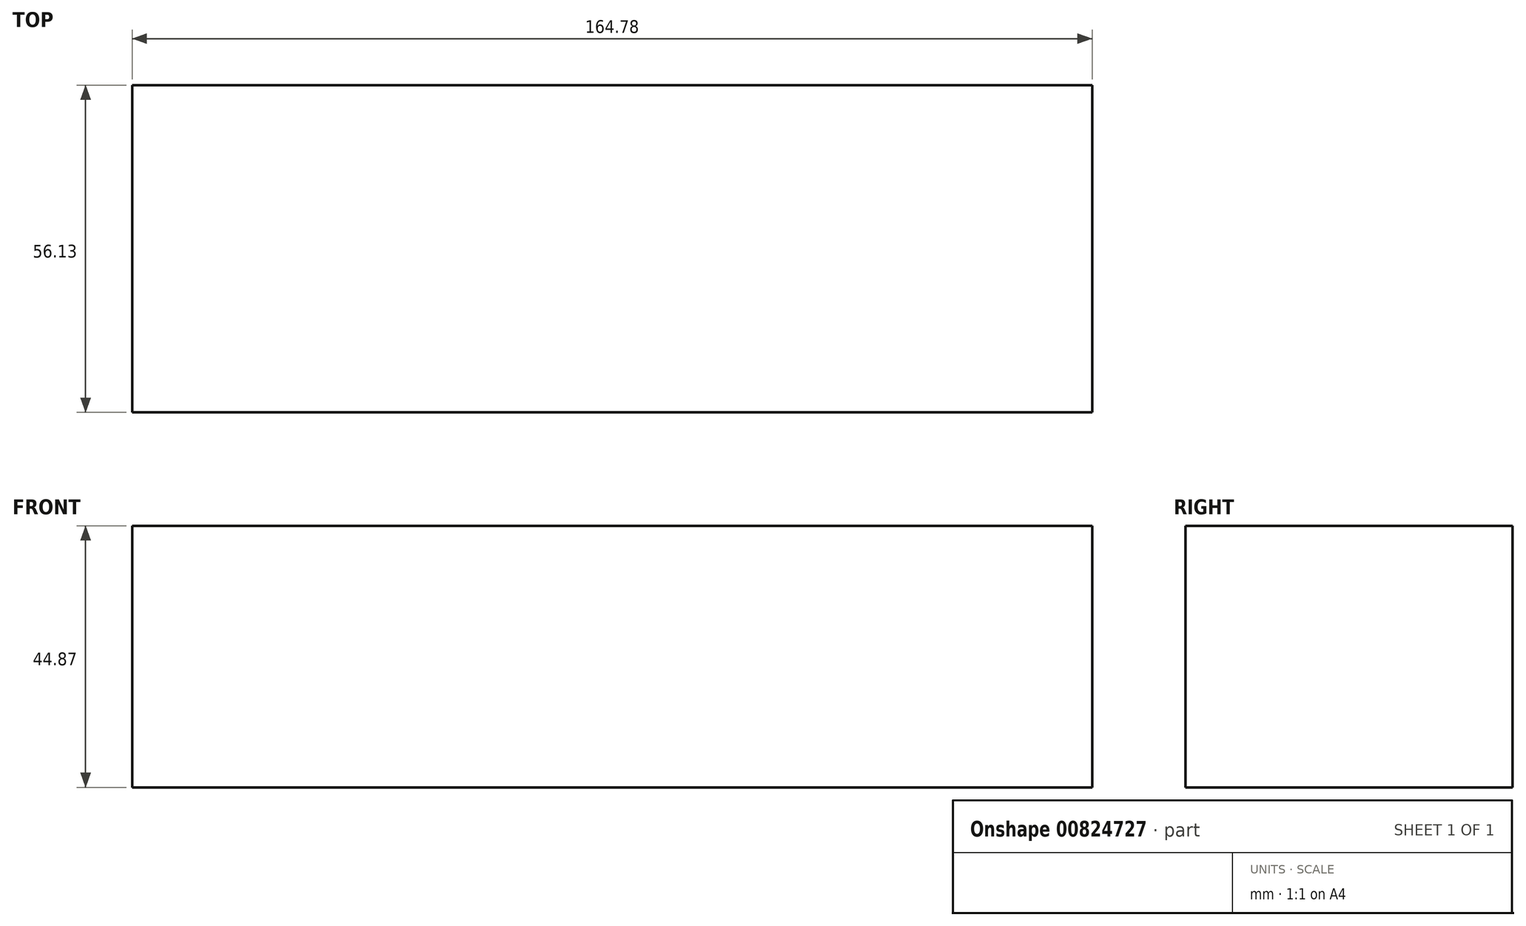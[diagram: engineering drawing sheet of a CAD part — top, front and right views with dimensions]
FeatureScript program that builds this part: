
annotation { "Feature Type Name" : "Feature", "Feature Type Description" : "" }
export const myFeature = defineFeature(function(context is Context, id is Id, definition is map)
    precondition{}
    {
        {
            var Q0;
            Q0=qCreatedBy(makeId("Front.planeOp"),FACE);
            var sketch = newSketch(context, id + "F0", { "sketchPlane" : qUnion([Q0])});
            skLineSegment(sketch, "E0.bottom", {"start": v(-83.62, 10.1) * mm, "end": v(81.16, 10.1) * mm});
            skLineSegment(sketch, "E0.top", {"start": v(-83.62, -34.76) * mm, "end": v(81.16, -34.76) * mm});
            skLineSegment(sketch, "E0.left", {"start": v(-83.62, 10.1) * mm, "end": v(-83.62, -34.76) * mm});
            skLineSegment(sketch, "E0.right", {"start": v(81.16, 10.1) * mm, "end": v(81.16, -34.76) * mm});
            skSolve(sketch);
        }
        {
            var Q0;
            Q0=makeQuery(id+"F0.imprint","IMPRINT",FACE,{"disambiguationData":[TD([[makeQuery(id+"F0.imprint","IMPRINT",EDGE,{"derivedFrom":sQuery(id+"F0.wireOp",EDGE,"E0.bottom")}),-1.0]])]});
            extrude(context, id + "F1", {"entities" : qUnion([Q0]), "depth" : 56.13 * mm, "offsetDistance" : 25.4 * mm});
        }
    });
